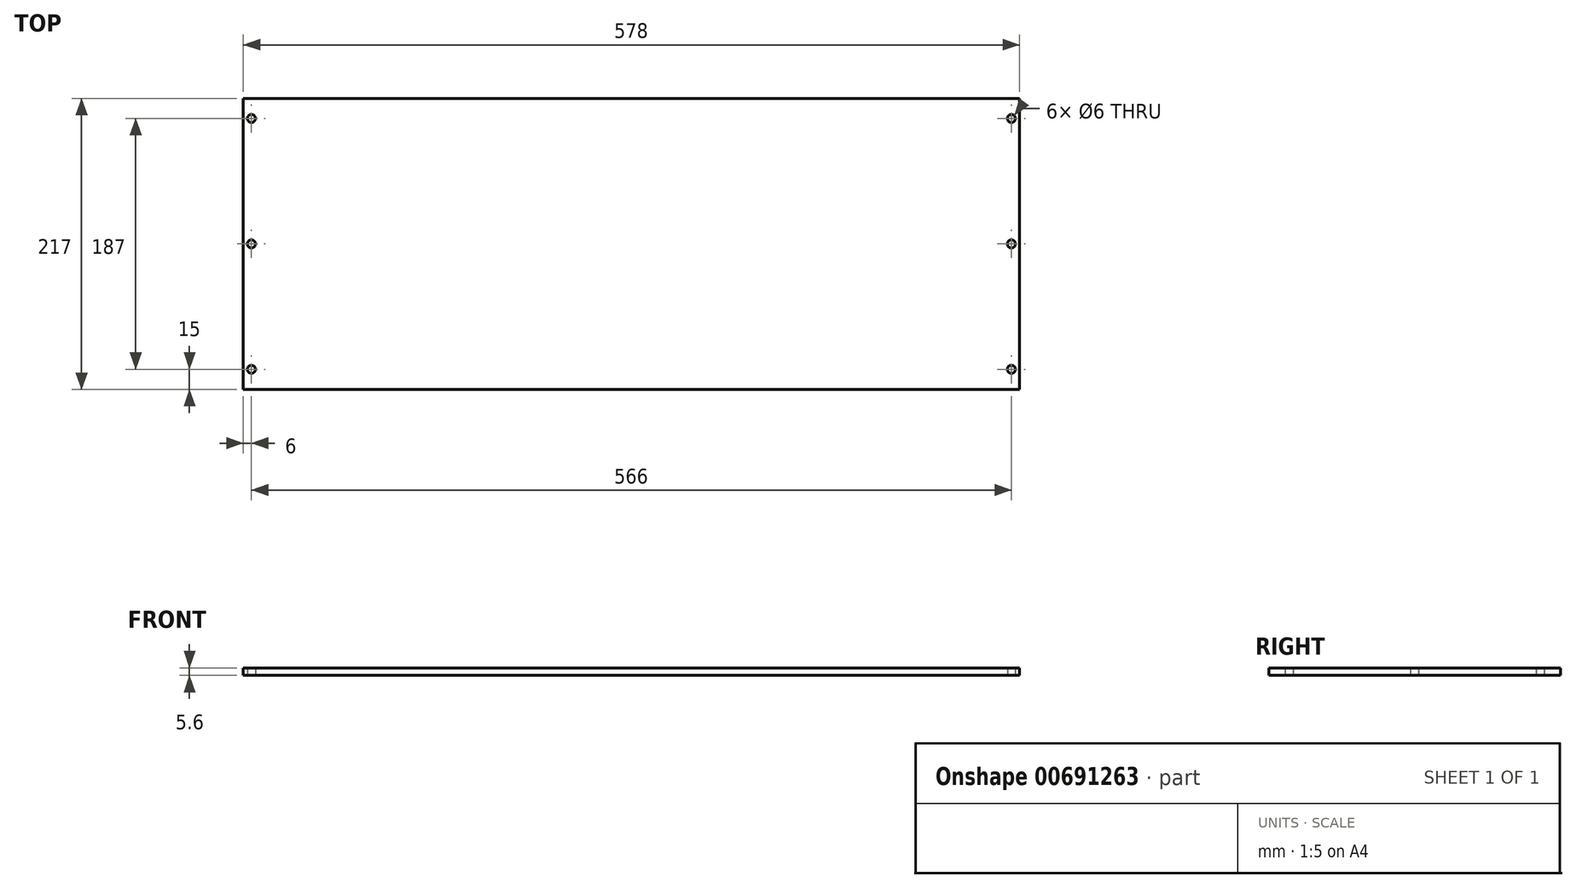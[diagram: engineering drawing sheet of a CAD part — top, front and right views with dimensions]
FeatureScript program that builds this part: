
annotation { "Feature Type Name" : "Feature", "Feature Type Description" : "" }
export const myFeature = defineFeature(function(context is Context, id is Id, definition is map)
    precondition{}
    {
        {
            var Q0;
            Q0=qCreatedBy(makeId("Top.planeOp"),FACE);
            var sketch = newSketch(context, id + "F0", { "sketchPlane" : qUnion([Q0])});
            skLineSegment(sketch, "E0.bottom", {"start": v(-289, 108.5) * mm, "end": v(289, 108.5) * mm});
            skLineSegment(sketch, "E0.top", {"start": v(-289, -108.5) * mm, "end": v(289, -108.5) * mm});
            skLineSegment(sketch, "E0.left", {"start": v(-289, 108.5) * mm, "end": v(-289, -108.5) * mm});
            skLineSegment(sketch, "E0.right", {"start": v(289, 108.5) * mm, "end": v(289, -108.5) * mm});
            skLineSegment(sketch, "E1", {"start": v(283, 108.5) * mm, "end": v(283, 0) * mm, "construction": true});
            skLineSegment(sketch, "E2", {"start": v(283, 0) * mm, "end": v(221.43, 0) * mm, "construction": true});
            skPoint(sketch, "E3.orphan", {"position": v(283, -108.5) * mm});
            skLineSegment(sketch, "E4", {"start": v(283, 0) * mm, "end": v(283, -108.5) * mm, "construction": true});
            skLineSegment(sketch, "E5", {"start": v(0, 108.5) * mm, "end": v(0, -108.5) * mm, "construction": true});
            skCircle(sketch, "E6", {"center": v(283, 0) * mm, "radius": 3 * mm});
            skCircle(sketch, "E7", {"center": v(283, 93.5) * mm, "radius": 3 * mm});
            skCircle(sketch, "E8", {"center": v(283, -93.5) * mm, "radius": 3 * mm});
            skCircle(sketch, "E9.MirrorC", {"center": v(-283, 93.5) * mm, "radius": 3 * mm});
            skCircle(sketch, "E10.MirrorC", {"center": v(-283, 0) * mm, "radius": 3 * mm});
            skCircle(sketch, "E11.MirrorC", {"center": v(-283, -93.5) * mm, "radius": 3 * mm});
            skLineSegment(sketch, "E12.bottom", {"start": v(-303.23, 123.08) * mm, "end": v(303.5, 123.08) * mm, "construction": true});
            skLineSegment(sketch, "E12.top", {"start": v(-303.23, -126.2) * mm, "end": v(303.5, -126.2) * mm, "construction": true});
            skLineSegment(sketch, "E12.left", {"start": v(-303.23, 123.08) * mm, "end": v(-303.23, -126.2) * mm, "construction": true});
            skLineSegment(sketch, "E12.right", {"start": v(303.5, 123.08) * mm, "end": v(303.5, -126.2) * mm, "construction": true});
            skSolve(sketch);
        }
        {
            var Q0;
            Q0 = qSketchRegion(id + "F0", true);
            extrude(context, id + "F1", {"entities" : qUnion([Q0]), "depth" : 5.6 * mm, "offsetDistance" : 25 * mm});
        }
    });
